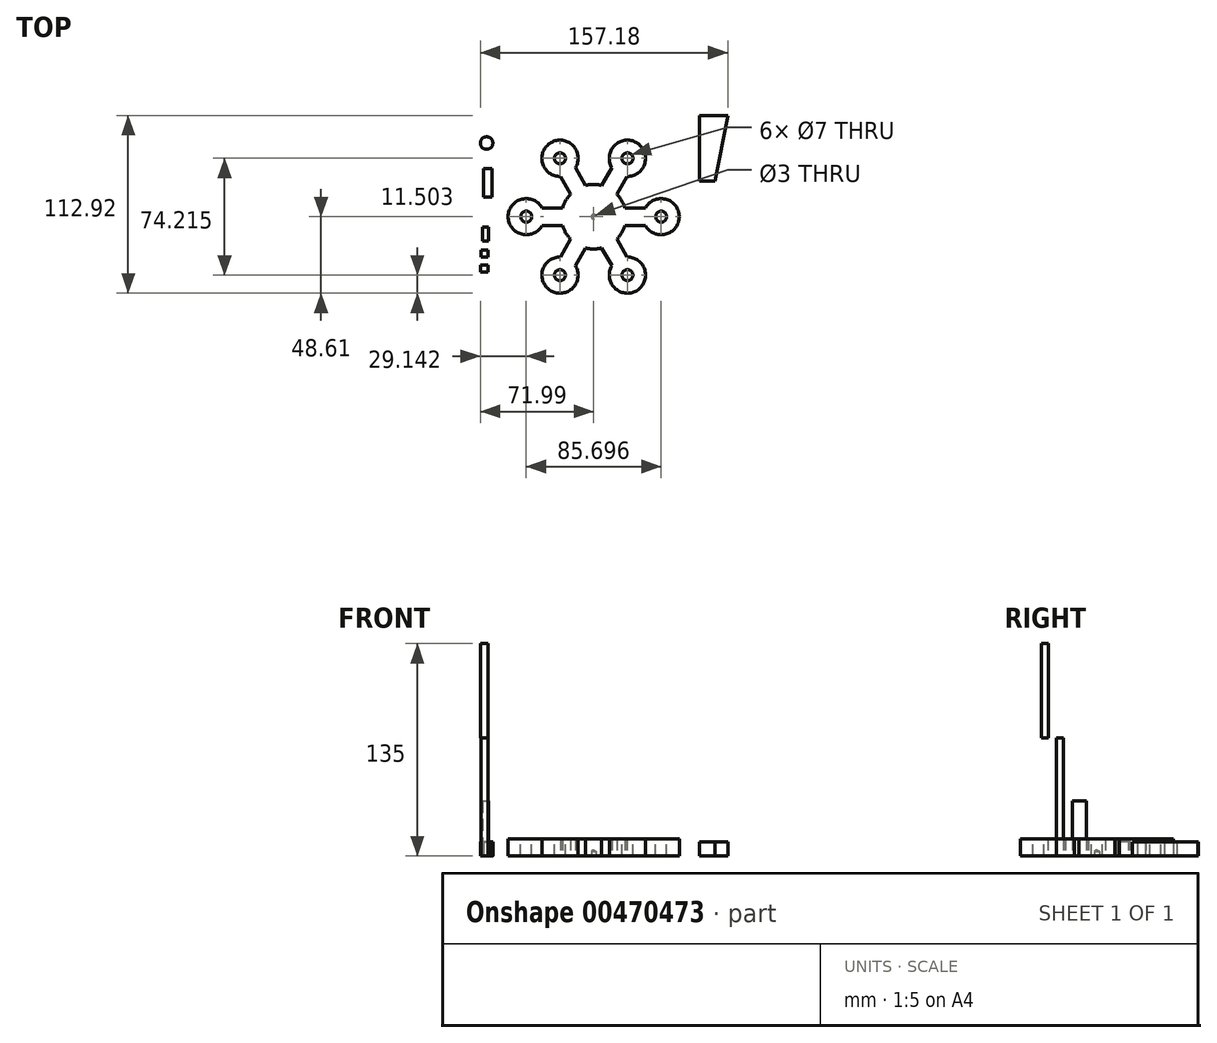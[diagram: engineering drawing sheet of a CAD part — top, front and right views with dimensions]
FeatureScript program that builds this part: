
annotation { "Feature Type Name" : "Feature", "Feature Type Description" : "" }
export const myFeature = defineFeature(function(context is Context, id is Id, definition is map)
    precondition{}
    {
        {
            var Q0;
            Q0=qCreatedBy(makeId("Top.planeOp"),FACE);
            var sketch = newSketch(context, id + "F0", { "sketchPlane" : qUnion([Q0])});
            skCircle(sketch, "E0", {"center": v(0, 0) * mm, "radius": 20.5 * mm});
            skLineSegment(sketch, "E1.bottom", {"start": v(-19.75, 5.5) * mm, "end": v(-32.75, 5.5) * mm});
            skLineSegment(sketch, "E1.top", {"start": v(-19.75, -5.5) * mm, "end": v(-32.75, -5.5) * mm});
            skLineSegment(sketch, "E1.left", {"start": v(-19.75, 5.5) * mm, "end": v(-19.75, -5.5) * mm});
            skLineSegment(sketch, "E1.right", {"start": v(-32.75, 5.5) * mm, "end": v(-32.75, -5.5) * mm});
            skCircle(sketch, "E2", {"center": v(-42.85, 0) * mm, "radius": 11.5 * mm});
            skLineSegment(sketch, "E3.1.0", {"start": v(-5.11, 19.85) * mm, "end": v(-11.61, 31.11) * mm});
            skLineSegment(sketch, "E3.1.1", {"start": v(-5.11, 19.85) * mm, "end": v(-14.64, 14.35) * mm});
            skLineSegment(sketch, "E3.1.2", {"start": v(-14.64, 14.35) * mm, "end": v(-21.14, 25.61) * mm});
            skLineSegment(sketch, "E3.1.3", {"start": v(-11.61, 31.11) * mm, "end": v(-21.14, 25.61) * mm});
            skCircle(sketch, "E3.1.4", {"center": v(-21.42, 37.1) * mm, "radius": 11.5 * mm});
            skLineSegment(sketch, "E3.2.0", {"start": v(14.64, 14.35) * mm, "end": v(21.14, 25.61) * mm});
            skLineSegment(sketch, "E3.2.1", {"start": v(14.64, 14.35) * mm, "end": v(5.11, 19.85) * mm});
            skLineSegment(sketch, "E3.2.2", {"start": v(5.11, 19.85) * mm, "end": v(11.61, 31.11) * mm});
            skLineSegment(sketch, "E3.2.3", {"start": v(21.14, 25.61) * mm, "end": v(11.61, 31.11) * mm});
            skCircle(sketch, "E3.2.4", {"center": v(21.42, 37.1) * mm, "radius": 11.5 * mm});
            skLineSegment(sketch, "E3.3.0", {"start": v(19.75, -5.5) * mm, "end": v(32.75, -5.5) * mm});
            skLineSegment(sketch, "E3.3.1", {"start": v(19.75, -5.5) * mm, "end": v(19.75, 5.5) * mm});
            skLineSegment(sketch, "E3.3.2", {"start": v(19.75, 5.5) * mm, "end": v(32.75, 5.5) * mm});
            skLineSegment(sketch, "E3.3.3", {"start": v(32.75, -5.5) * mm, "end": v(32.75, 5.5) * mm});
            skCircle(sketch, "E3.3.4", {"center": v(42.85, 0) * mm, "radius": 11.5 * mm});
            skLineSegment(sketch, "E3.4.0", {"start": v(5.11, -19.85) * mm, "end": v(11.61, -31.11) * mm});
            skLineSegment(sketch, "E3.4.1", {"start": v(5.11, -19.85) * mm, "end": v(14.64, -14.35) * mm});
            skLineSegment(sketch, "E3.4.2", {"start": v(14.64, -14.35) * mm, "end": v(21.14, -25.61) * mm});
            skLineSegment(sketch, "E3.4.3", {"start": v(11.61, -31.11) * mm, "end": v(21.14, -25.61) * mm});
            skCircle(sketch, "E3.4.4", {"center": v(21.42, -37.1) * mm, "radius": 11.5 * mm});
            skLineSegment(sketch, "E3.5.0", {"start": v(-14.64, -14.35) * mm, "end": v(-21.14, -25.61) * mm});
            skLineSegment(sketch, "E3.5.1", {"start": v(-14.64, -14.35) * mm, "end": v(-5.11, -19.85) * mm});
            skLineSegment(sketch, "E3.5.2", {"start": v(-5.11, -19.85) * mm, "end": v(-11.61, -31.11) * mm});
            skLineSegment(sketch, "E3.5.3", {"start": v(-21.14, -25.61) * mm, "end": v(-11.61, -31.11) * mm});
            skCircle(sketch, "E3.5.4", {"center": v(-21.42, -37.1) * mm, "radius": 11.5 * mm});
            skLineSegment(sketch, "E3.anchor1", {"start": v(0, 0) * mm, "end": v(-32.75, 5.5) * mm, "construction": true});
            skLineSegment(sketch, "E3.anchor2", {"start": v(0, 0) * mm, "end": v(-21.14, -25.61) * mm, "construction": true});
            skSolve(sketch);
        }
        {
            var Q0;
            Q0 = qSketchRegion(id + "F0", true);
            extrude(context, id + "F1", {"entities" : qUnion([Q0]), "depth" : 11 * mm});
        }
        {
            var Q0;
            Q0=makeQuery(id+"F1.opExtrude","CAP_FACE",FACE,{"disambiguationData":[OSD([sQuery(id+"F0.wireOp",EDGE,"E0"),sQuery(id+"F0.wireOp",EDGE,"E1.bottom"),sQuery(id+"F0.wireOp",EDGE,"E1.top"),sQuery(id+"F0.wireOp",EDGE,"E2"),sQuery(id+"F0.wireOp",EDGE,"E3.1.0"),sQuery(id+"F0.wireOp",EDGE,"E3.1.2"),sQuery(id+"F0.wireOp",EDGE,"E3.1.4"),sQuery(id+"F0.wireOp",EDGE,"E3.2.0"),sQuery(id+"F0.wireOp",EDGE,"E3.2.2"),sQuery(id+"F0.wireOp",EDGE,"E3.2.4"),sQuery(id+"F0.wireOp",EDGE,"E3.3.0"),sQuery(id+"F0.wireOp",EDGE,"E3.3.2"),sQuery(id+"F0.wireOp",EDGE,"E3.3.4"),sQuery(id+"F0.wireOp",EDGE,"E3.4.0"),sQuery(id+"F0.wireOp",EDGE,"E3.4.2"),sQuery(id+"F0.wireOp",EDGE,"E3.4.4"),sQuery(id+"F0.wireOp",EDGE,"E3.5.0"),sQuery(id+"F0.wireOp",EDGE,"E3.5.2"),sQuery(id+"F0.wireOp",EDGE,"E3.5.4")])],"isStart":false});
            var sketch = newSketch(context, id + "F2", { "sketchPlane" : qUnion([Q0])});
            skPoint(sketch, "E4", {"position": v(-21.42, 37.1) * mm});
            skPoint(sketch, "E5", {"position": v(21.42, 37.1) * mm});
            skPoint(sketch, "E6", {"position": v(42.85, 0) * mm});
            skPoint(sketch, "E7", {"position": v(21.42, -37.1) * mm});
            skPoint(sketch, "E8", {"position": v(-42.85, 0) * mm});
            skPoint(sketch, "E9", {"position": v(-21.42, -37.1) * mm});
            skSolve(sketch);
        }
        {
            var Q0;
            Q0=sQuery(id+"F2.wireOp",VERTEX,"E4");
            var Q1;
            Q1=sQuery(id+"F2.wireOp",VERTEX,"E5");
            var Q2;
            Q2=sQuery(id+"F2.wireOp",VERTEX,"E6");
            var Q3;
            Q3=sQuery(id+"F2.wireOp",VERTEX,"E7");
            var Q4;
            Q4=sQuery(id+"F2.wireOp",VERTEX,"E9");
            var Q5;
            Q5=sQuery(id+"F2.wireOp",VERTEX,"E8");
            var Q6;
            Q6=makeQuery(id+"F1.opExtrude","SWEPT_BODY",BODY,{"disambiguationData":[OSD([sQuery(id+"F0.wireOp",EDGE,"E0"),sQuery(id+"F0.wireOp",EDGE,"E1.bottom"),sQuery(id+"F0.wireOp",EDGE,"E1.top"),sQuery(id+"F0.wireOp",EDGE,"E2"),sQuery(id+"F0.wireOp",EDGE,"E3.1.0"),sQuery(id+"F0.wireOp",EDGE,"E3.1.2"),sQuery(id+"F0.wireOp",EDGE,"E3.1.4"),sQuery(id+"F0.wireOp",EDGE,"E3.2.0"),sQuery(id+"F0.wireOp",EDGE,"E3.2.2"),sQuery(id+"F0.wireOp",EDGE,"E3.2.4"),sQuery(id+"F0.wireOp",EDGE,"E3.3.0"),sQuery(id+"F0.wireOp",EDGE,"E3.3.2"),sQuery(id+"F0.wireOp",EDGE,"E3.3.4"),sQuery(id+"F0.wireOp",EDGE,"E3.4.0"),sQuery(id+"F0.wireOp",EDGE,"E3.4.2"),sQuery(id+"F0.wireOp",EDGE,"E3.4.4"),sQuery(id+"F0.wireOp",EDGE,"E3.5.0"),sQuery(id+"F0.wireOp",EDGE,"E3.5.2"),sQuery(id+"F0.wireOp",EDGE,"E3.5.4")])]});
            hole(context, id + "F3", {"style" : HoleStyle.SIMPLE, "endStyle" : HoleEndStyle.THROUGH, "holeDiameter" : 7 * mm, "isTappedThrough" : true, "tappedDepth" : 12 * mm, "tapClearance" : 3, "startFromSketch" : true, "locations" : qUnion([Q0, Q1, Q2, Q3, Q4, Q5]), "scope" : qUnion([Q6])});
        }
        {
            var Q0;
            Q0=qCreatedBy(makeId("Top.planeOp"),FACE);
            var sketch = newSketch(context, id + "F4", { "sketchPlane" : qUnion([Q0])});
            skPoint(sketch, "E10", {"position": v(0, 0) * mm});
            skSolve(sketch);
        }
        {
            var Q0;
            Q0=sQuery(id+"F4.wireOp",VERTEX,"E10");
            var Q1;
            Q1=makeQuery(id+"F1.opExtrude","SWEPT_BODY",BODY,{"disambiguationData":[OSD([sQuery(id+"F0.wireOp",EDGE,"E0"),sQuery(id+"F0.wireOp",EDGE,"E1.bottom"),sQuery(id+"F0.wireOp",EDGE,"E1.top"),sQuery(id+"F0.wireOp",EDGE,"E2"),sQuery(id+"F0.wireOp",EDGE,"E3.1.0"),sQuery(id+"F0.wireOp",EDGE,"E3.1.2"),sQuery(id+"F0.wireOp",EDGE,"E3.1.4"),sQuery(id+"F0.wireOp",EDGE,"E3.2.0"),sQuery(id+"F0.wireOp",EDGE,"E3.2.2"),sQuery(id+"F0.wireOp",EDGE,"E3.2.4"),sQuery(id+"F0.wireOp",EDGE,"E3.3.0"),sQuery(id+"F0.wireOp",EDGE,"E3.3.2"),sQuery(id+"F0.wireOp",EDGE,"E3.3.4"),sQuery(id+"F0.wireOp",EDGE,"E3.4.0"),sQuery(id+"F0.wireOp",EDGE,"E3.4.2"),sQuery(id+"F0.wireOp",EDGE,"E3.4.4"),sQuery(id+"F0.wireOp",EDGE,"E3.5.0"),sQuery(id+"F0.wireOp",EDGE,"E3.5.2"),sQuery(id+"F0.wireOp",EDGE,"E3.5.4")])]});
            hole(context, id + "F5", {"style" : HoleStyle.SIMPLE, "endStyle" : HoleEndStyle.BLIND, "oppositeDirection" : true, "holeDiameter" : 3 * mm, "majorDiameter" : 5 * mm, "holeDepth" : 3 * mm, "isTappedThrough" : true, "tappedDepth" : 12 * mm, "tapClearance" : 3, "startFromSketch" : true, "locations" : qUnion([Q0]), "scope" : qUnion([Q1])});
        }
        {
            var Q0;
            Q0=qCreatedBy(makeId("Top.planeOp"),FACE);
            var sketch = newSketch(context, id + "F6", { "sketchPlane" : qUnion([Q0])});
            skCircle(sketch, "E11", {"center": v(-68.01, 46.78) * mm, "radius": 3.98 * mm});
            skSolve(sketch);
        }
        {
            var Q0;
            Q0 = qSketchRegion(id + "F6", true);
            extrude(context, id + "F7", {"entities" : qUnion([Q0]), "depth" : 9 * mm, "offsetDistance" : 25 * mm});
        }
        {
            var Q0;
            Q0=qCreatedBy(makeId("Top.planeOp"),FACE);
            var sketch = newSketch(context, id + "F8", { "sketchPlane" : qUnion([Q0])});
            skLineSegment(sketch, "E12.bottom", {"start": v(-70.07, 30.72) * mm, "end": v(-64.6, 30.72) * mm});
            skLineSegment(sketch, "E12.top", {"start": v(-70.07, 12.6) * mm, "end": v(-64.6, 12.6) * mm});
            skLineSegment(sketch, "E12.left", {"start": v(-70.07, 30.72) * mm, "end": v(-70.07, 12.6) * mm});
            skLineSegment(sketch, "E12.right", {"start": v(-64.6, 30.72) * mm, "end": v(-64.6, 12.6) * mm});
            skSolve(sketch);
        }
        {
            var Q0;
            Q0 = qSketchRegion(id + "F8", true);
            extrude(context, id + "F9", {"entities" : qUnion([Q0]), "depth" : 9 * mm, "offsetDistance" : 25 * mm});
        }
        {
            var Q0;
            Q0=qCreatedBy(makeId("Top.planeOp"),FACE);
            var sketch = newSketch(context, id + "F10", { "sketchPlane" : qUnion([Q0])});
            skLineSegment(sketch, "E13.bottom", {"start": v(-71.7, -21.28) * mm, "end": v(-67.2, -21.28) * mm});
            skLineSegment(sketch, "E13.top", {"start": v(-71.7, -25.78) * mm, "end": v(-67.2, -25.78) * mm});
            skLineSegment(sketch, "E13.left", {"start": v(-71.7, -21.28) * mm, "end": v(-71.7, -25.78) * mm});
            skLineSegment(sketch, "E13.right", {"start": v(-67.2, -21.28) * mm, "end": v(-67.2, -25.78) * mm});
            skSolve(sketch);
        }
        {
            var Q0;
            Q0 = qSketchRegion(id + "F10", true);
            extrude(context, id + "F11", {"entities" : qUnion([Q0]), "depth" : 75 * mm, "offsetDistance" : 25 * mm});
        }
        {
            var Q0;
            Q0=qCreatedBy(makeId("Top.planeOp"),FACE);
            var sketch = newSketch(context, id + "F12", { "sketchPlane" : qUnion([Q0])});
            skLineSegment(sketch, "E14.bottom", {"start": v(-70.77, -6.62) * mm, "end": v(-66.77, -6.62) * mm});
            skLineSegment(sketch, "E14.top", {"start": v(-70.77, -15.62) * mm, "end": v(-66.77, -15.62) * mm});
            skLineSegment(sketch, "E14.left", {"start": v(-70.77, -6.62) * mm, "end": v(-70.77, -15.62) * mm});
            skLineSegment(sketch, "E14.right", {"start": v(-66.77, -6.62) * mm, "end": v(-66.77, -15.62) * mm});
            skSolve(sketch);
        }
        {
            var Q0;
            Q0 = qSketchRegion(id + "F12", true);
            extrude(context, id + "F13", {"entities" : qUnion([Q0]), "depth" : 35 * mm, "offsetDistance" : 25 * mm});
        }
        {
            var Q0;
            Q0=makeQuery(id+"F11.opExtrude","CAP_FACE",FACE,{"disambiguationData":[OSD([sQuery(id+"F10.wireOp",EDGE,"E13.bottom"),sQuery(id+"F10.wireOp",EDGE,"E13.top"),sQuery(id+"F10.wireOp",EDGE,"E13.left"),sQuery(id+"F10.wireOp",EDGE,"E13.right")])],"isStart":false});
            var sketch = newSketch(context, id + "F14", { "sketchPlane" : qUnion([Q0])});
            skLineSegment(sketch, "E15.bottom", {"start": v(-71.74, -30.7) * mm, "end": v(-67.24, -30.7) * mm});
            skLineSegment(sketch, "E15.top", {"start": v(-71.74, -35.2) * mm, "end": v(-67.24, -35.2) * mm});
            skLineSegment(sketch, "E15.left", {"start": v(-71.74, -30.7) * mm, "end": v(-71.74, -35.2) * mm});
            skLineSegment(sketch, "E15.right", {"start": v(-67.24, -30.7) * mm, "end": v(-67.24, -35.2) * mm});
            skSolve(sketch);
        }
        {
            var Q0;
            Q0 = qSketchRegion(id + "F14", true);
            extrude(context, id + "F15", {"entities" : qUnion([Q0]), "depth" : 60 * mm, "offsetDistance" : 25 * mm});
        }
        {
            var Q0;
            Q0=qCreatedBy(makeId("Top.planeOp"),FACE);
            var sketch = newSketch(context, id + "F16", { "sketchPlane" : qUnion([Q0])});
            skLineSegment(sketch, "E16", {"start": v(67.27, 64.3) * mm, "end": v(67.27, 22.59) * mm});
            skLineSegment(sketch, "E17", {"start": v(67.27, 22.59) * mm, "end": v(76.9, 22.59) * mm});
            skLineSegment(sketch, "E18", {"start": v(76.9, 22.59) * mm, "end": v(85.2, 64.19) * mm});
            skLineSegment(sketch, "E19", {"start": v(85.2, 64.19) * mm, "end": v(67.27, 64.3) * mm});
            skSolve(sketch);
        }
        {
            var Q0;
            Q0 = qSketchRegion(id + "F16", true);
            extrude(context, id + "F17", {"entities" : qUnion([Q0]), "depth" : 9 * mm, "offsetDistance" : 25 * mm});
        }
    });
